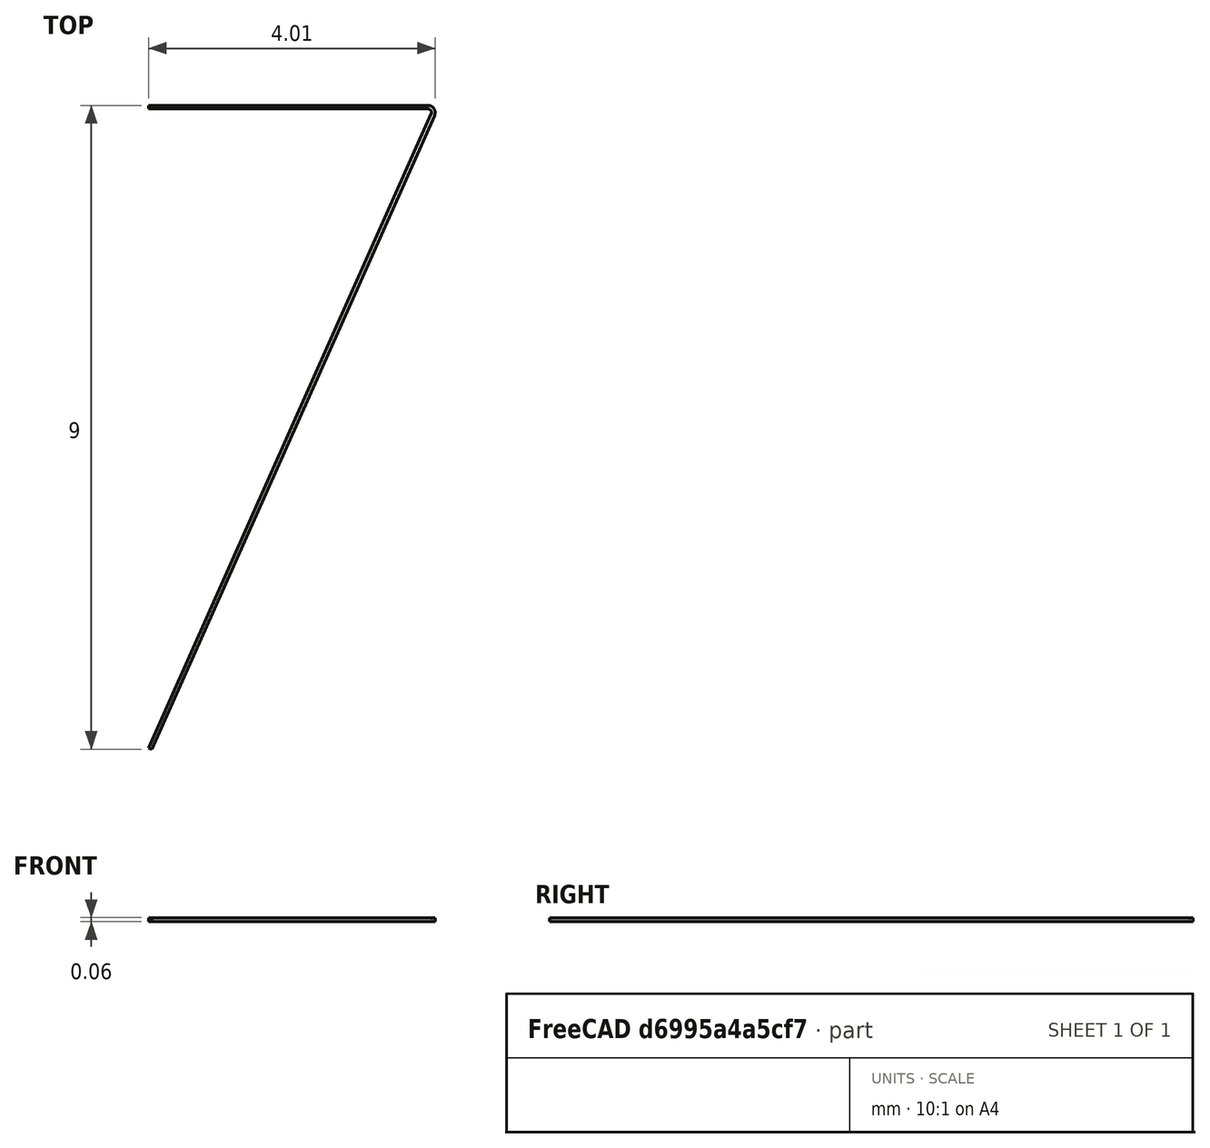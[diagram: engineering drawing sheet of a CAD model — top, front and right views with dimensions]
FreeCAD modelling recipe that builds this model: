
FCSTD DOCUMENT  (FreeCAD 0.16R6712 (Git))
Label: 7t
License: All rights reserved
LicenseURL: http://en.wikipedia.org/wiki/All_rights_reserved
objects: Sketcher::SketchObject×1, PartDesign::Pad×1, Mesh::Feature×1
note: 3 computed .brp shape members not serialized (recipe doc carries the construction recipe); baked Part::Feature solids carry a one-line shape summary decoded from their .brp

FEATURE [Sketcher::SketchObject] Sketch
  sketch-geometry (8):
    g0: LineSegment StartX=-2 StartY=9 StartZ=0 EndX=1.90868 EndY=9 EndZ=0
    g1: LineSegment StartX=2 StartY=8.85924 StartZ=0 EndX=-1.95434 EndY=0 EndZ=0
    g2: LineSegment StartX=-2 StartY=9 StartZ=0 EndX=-2 EndY=8.95 EndZ=0
    g3: LineSegment StartX=-2 StartY=8.95 StartZ=0 EndX=1.90868 EndY=8.95 EndZ=0
    g4: LineSegment StartX=1.95434 StartY=8.87962 StartZ=0 EndX=-2 EndY=0.0203796 EndZ=0
    g5: LineSegment StartX=-2 StartY=0.0203796 StartZ=0 EndX=-1.95434 EndY=0 EndZ=0
    g6: ArcOfCircle CenterX=1.90868 CenterY=8.9 CenterZ=0 NormalX=0 NormalY=0 NormalZ=1 Radius=0.05 StartAngle=5.86337 EndAngle=7.85398
    g7: ArcOfCircle CenterX=1.90868 CenterY=8.9 CenterZ=0 NormalX=0 NormalY=0 NormalZ=1 Radius=0.1 StartAngle=5.86337 EndAngle=7.85398
  constraints (22):
    c: Horizontal(g0)
    c: PointOnObject(g1,g-1)
    c: Coincident(g2,g0)
    c: Coincident(g3,g2)
    c: Horizontal(g3)
    c: Coincident(g5,g1)
    c: Coincident(g4,g5)
    c: Distance(g2,g0) = 0.05
    c: Distance(g1,g4) = 0.05
    c: Perpendicular(g5,g4)
    c: Perpendicular(g3,g2)
    c: DistanceX(g-2,g0) = -2
    c: DistanceX(g-2,g4) = -2
    c: Perpendicular(g5,g1)
    c: Tangent(g3,g6) = 1.5708
    c: Tangent(g4,g6) = 1.5708
    c: Tangent(g0,g7) = 1.5708
    c: Tangent(g1,g7) = 1.5708
    c: Radius(g6) = 0.05
    c: Radius(g7) = 0.1
    c: DistanceY(g-1,g0) = 9
    c: DistanceX(g-2,g1) = 2
FEATURE [PartDesign::Pad] Pad
  Length = 0.05
  Length2 = 100
  Midplane = true
  Sketch = -> Sketch
  Type = 0
FEATURE [Mesh::Feature] Mesh  label="Pad (Meshed)"
